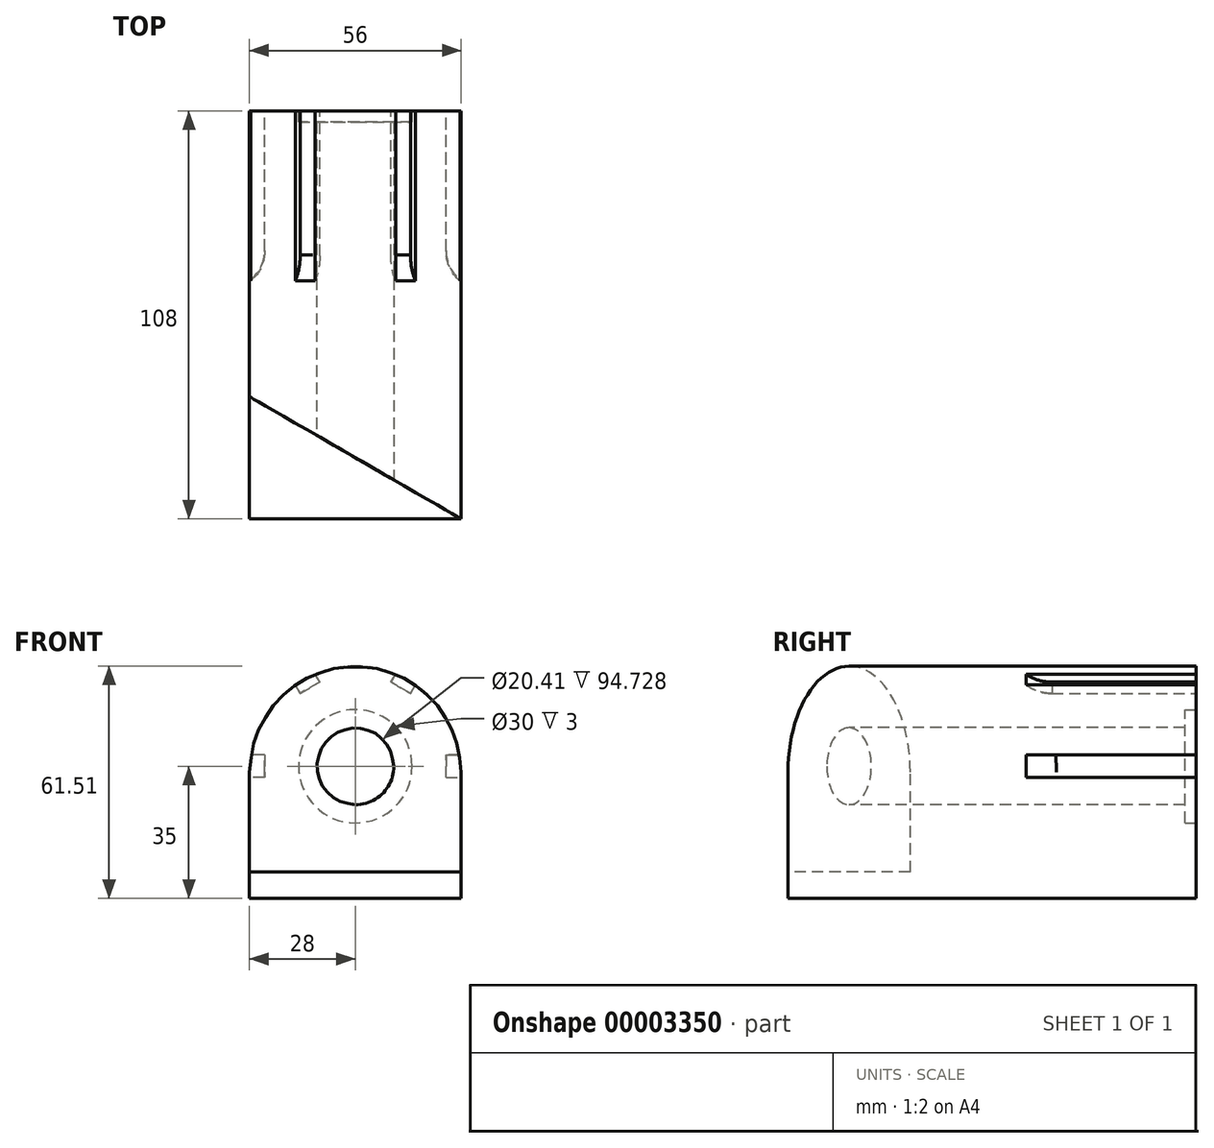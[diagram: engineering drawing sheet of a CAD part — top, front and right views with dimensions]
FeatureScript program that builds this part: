
annotation { "Feature Type Name" : "Feature", "Feature Type Description" : "" }
export const myFeature = defineFeature(function(context is Context, id is Id, definition is map)
    precondition{}
    {
        {
            var Q0;
            Q0=qCreatedBy(makeId("Front.planeOp"),FACE);
            var sketch = newSketch(context, id + "F0", { "sketchPlane" : qUnion([Q0])});
            skArc(sketch, "E0", {"start": v(28, -1.5) * mm, "mid": v(0, 26.5) * mm, "end": v(-28, -1.5) * mm});
            skLineSegment(sketch, "E1", {"start": v(-28, 0) * mm, "end": v(-28, -35) * mm});
            skLineSegment(sketch, "E2.0.MirrorCS", {"start": v(28, 0) * mm, "end": v(28, -35) * mm});
            skLineSegment(sketch, "E3", {"start": v(-28, -35) * mm, "end": v(28, -35) * mm});
            skLineSegment(sketch, "E4", {"start": v(-24, 0) * mm, "end": v(-24, -3) * mm});
            skLineSegment(sketch, "E5", {"start": v(-24, -3) * mm, "end": v(-28, -3) * mm});
            skLineSegment(sketch, "E6.0.MirrorCS", {"start": v(-24, 0) * mm, "end": v(-24, 3) * mm});
            skLineSegment(sketch, "E7.0.MirrorCS", {"start": v(-24, 3) * mm, "end": v(-27.64, 3) * mm});
            skPoint(sketch, "E8.orphan", {"position": v(-28, 3) * mm});
            skLineSegment(sketch, "E9.0.MirrorCS", {"start": v(24, 3) * mm, "end": v(27.64, 3) * mm});
            skLineSegment(sketch, "E10.0.MirrorCS", {"start": v(24, 0) * mm, "end": v(24, 3) * mm});
            skLineSegment(sketch, "E11.0.MirrorCS", {"start": v(24, 0) * mm, "end": v(24, -3) * mm});
            skLineSegment(sketch, "E12.0.MirrorCS", {"start": v(24, -3) * mm, "end": v(28, -3) * mm});
            skLineSegment(sketch, "E13", {"start": v(0, 0) * mm, "end": v(-15.25, 26.4) * mm, "construction": true});
            skLineSegment(sketch, "E14.0.MirrorCS", {"start": v(0, 0) * mm, "end": v(15.25, 26.4) * mm, "construction": true});
            skLineSegment(sketch, "E15.0.MirrorCS", {"start": v(9.4, 22.28) * mm, "end": v(10.63, 24.41) * mm});
            skLineSegment(sketch, "E16.0.MirrorCS", {"start": v(12, 20.78) * mm, "end": v(9.4, 22.28) * mm});
            skLineSegment(sketch, "E17.0.MirrorCS", {"start": v(12, 20.78) * mm, "end": v(14.6, 19.28) * mm});
            skLineSegment(sketch, "E18.0.MirrorCS", {"start": v(14.6, 19.28) * mm, "end": v(15.9, 21.55) * mm});
            skLineSegment(sketch, "E19.0.MirrorCS", {"start": v(-9.4, 22.28) * mm, "end": v(-10.63, 24.41) * mm});
            skLineSegment(sketch, "E20.0.MirrorCS", {"start": v(-12, 20.78) * mm, "end": v(-9.4, 22.28) * mm});
            skLineSegment(sketch, "E21.0.MirrorCS", {"start": v(-12, 20.78) * mm, "end": v(-14.6, 19.28) * mm});
            skLineSegment(sketch, "E22.0.MirrorCS", {"start": v(-14.6, 19.28) * mm, "end": v(-15.9, 21.55) * mm});
            skPoint(sketch, "E23.orphan", {"position": v(-16.6, 22.75) * mm});
            skPoint(sketch, "E24.orphan", {"position": v(-11.22, 25.43) * mm});
            skPoint(sketch, "E25.orphan", {"position": v(11.22, 25.43) * mm});
            skPoint(sketch, "E26.orphan", {"position": v(16.6, 22.75) * mm});
            skSolve(sketch);
        }
        {
            var Q0;
            Q0=makeQuery(id+"F0.imprint","IMPRINT",FACE,{"disambiguationData":[TD([[makeQuery(id+"F0.imprint","IMPRINT",EDGE,{"derivedFrom":sQuery(id+"F0.wireOp",EDGE,"E4")}),-1.0]])]});
            var Q1;
            {var subQ6=sQuery(id+"F0.wireOp",EDGE,"E3");Q1=makeQuery(id+"F0.imprint","IMPRINT",FACE,{"disambiguationData":[TD([[makeQuery(id+"F0.imprint","IMPRINT",EDGE,{"derivedFrom":subQ6}),1.0]])]});}
            var Q2;
            {var subQ1=sQuery(id+"F0.wireOp",EDGE,"E19.0.MirrorCS");Q2=makeQuery(id+"F0.imprint","IMPRINT",FACE,{"disambiguationData":[TD([[makeQuery(id+"F0.imprint","IMPRINT",EDGE,{"derivedFrom":subQ1}),1.0]])]});}
            var Q3;
            {var subQ1=sQuery(id+"F0.wireOp",EDGE,"E9.0.MirrorCS");Q3=makeQuery(id+"F0.imprint","IMPRINT",FACE,{"disambiguationData":[TD([[makeQuery(id+"F0.imprint","IMPRINT",EDGE,{"derivedFrom":subQ1}),-1.0]])]});}
            var Q4;
            {var subQ1=sQuery(id+"F0.wireOp",EDGE,"E15.0.MirrorCS");Q4=makeQuery(id+"F0.imprint","IMPRINT",FACE,{"disambiguationData":[TD([[makeQuery(id+"F0.imprint","IMPRINT",EDGE,{"derivedFrom":subQ1}),-1.0]])]});}
            extrude(context, id + "F1", {"entities" : qUnion([Q0, Q1, Q2, Q3, Q4]), "depth" : 108 * mm});
        }
        {
            var Q0;
            Q0=makeQuery(id+"F0.imprint","IMPRINT",FACE,{"disambiguationData":[TD([[makeQuery(id+"F0.imprint","IMPRINT",EDGE,{"derivedFrom":sQuery(id+"F0.wireOp",EDGE,"E4")}),-1.0]])]});
            var Q1;
            {var subQ1=sQuery(id+"F0.wireOp",EDGE,"E19.0.MirrorCS");Q1=makeQuery(id+"F0.imprint","IMPRINT",FACE,{"disambiguationData":[TD([[makeQuery(id+"F0.imprint","IMPRINT",EDGE,{"derivedFrom":subQ1}),1.0]])]});}
            var Q2;
            {var subQ1=sQuery(id+"F0.wireOp",EDGE,"E15.0.MirrorCS");Q2=makeQuery(id+"F0.imprint","IMPRINT",FACE,{"disambiguationData":[TD([[makeQuery(id+"F0.imprint","IMPRINT",EDGE,{"derivedFrom":subQ1}),-1.0]])]});}
            var Q3;
            {var subQ1=sQuery(id+"F0.wireOp",EDGE,"E9.0.MirrorCS");Q3=makeQuery(id+"F0.imprint","IMPRINT",FACE,{"disambiguationData":[TD([[makeQuery(id+"F0.imprint","IMPRINT",EDGE,{"derivedFrom":subQ1}),-1.0]])]});}
            extrude(context, id + "F2", {"entities" : qUnion([Q0, Q1, Q2, Q3]), "operationType" : NewBodyOperationType.REMOVE, "depth" : 45 * mm});
        }
        {
            var Q0;
            Q0=makeQuery(id+"F2.boolean.opBoolean","COPY",EDGE,{"derivedFrom":makeQuery(id+"F2.opExtrude","CAP_EDGE",EDGE,{"disambiguationData":[OSD([sQuery(id+"F0.wireOp",EDGE,"E16.0.MirrorCS"),sQuery(id+"F0.wireOp",EDGE,"E17.0.MirrorCS")])],"isStart":false})});
            var Q1;
            Q1=makeQuery(id+"F2.boolean.opBoolean","COPY",EDGE,{"derivedFrom":makeQuery(id+"F2.opExtrude","CAP_EDGE",EDGE,{"disambiguationData":[OSD([sQuery(id+"F0.wireOp",EDGE,"E10.0.MirrorCS"),sQuery(id+"F0.wireOp",EDGE,"E11.0.MirrorCS")])],"isStart":false})});
            var Q2;
            Q2=makeQuery(id+"F2.boolean.opBoolean","COPY",EDGE,{"derivedFrom":makeQuery(id+"F2.opExtrude","CAP_EDGE",EDGE,{"disambiguationData":[OSD([sQuery(id+"F0.wireOp",EDGE,"E20.0.MirrorCS"),sQuery(id+"F0.wireOp",EDGE,"E21.0.MirrorCS")])],"isStart":false})});
            var Q3;
            Q3=makeQuery(id+"F2.boolean.opBoolean","COPY",EDGE,{"derivedFrom":makeQuery(id+"F2.opExtrude","CAP_EDGE",EDGE,{"disambiguationData":[OSD([sQuery(id+"F0.wireOp",EDGE,"E4"),sQuery(id+"F0.wireOp",EDGE,"E6.0.MirrorCS")])],"isStart":false})});
            fillet(context, id + "F3", {"entities" : qUnion([Q0, Q1, Q2, Q3]), "radius" : 10 * mm, "tangentPropagation" : true, "allowEdgeOverflow" : false});
        }
        {
            var Q0;
            {var subQ6=sQuery(id+"F0.wireOp",EDGE,"E3");Q0=makeQuery(id+"F0.imprint","IMPRINT",FACE,{"disambiguationData":[TD([[makeQuery(id+"F0.imprint","IMPRINT",EDGE,{"derivedFrom":subQ6}),1.0]])]});}
            var sketch = newSketch(context, id + "F4", { "sketchPlane" : qUnion([Q0])});
            skCircle(sketch, "E27", {"center": v(0, 0) * mm, "radius": 15 * mm});
            skSolve(sketch);
        }
        {
            var Q0;
            Q0 = qSketchRegion(id + "F4", true);
            extrude(context, id + "F5", {"entities" : qUnion([Q0]), "operationType" : NewBodyOperationType.REMOVE, "depth" : 3 * mm});
        }
        {
            var Q0;
            Q0=makeQuery(id+"F1.opExtrude","CAP_FACE",FACE,{"disambiguationData":[OSD([sQuery(id+"F0.wireOp",EDGE,"E0"),sQuery(id+"F0.wireOp",EDGE,"E1"),sQuery(id+"F0.wireOp",EDGE,"E2.0.MirrorCS"),sQuery(id+"F0.wireOp",EDGE,"E3")])],"isStart":false});
            var sketch = newSketch(context, id + "F6", { "sketchPlane" : qUnion([Q0])});
            skCircle(sketch, "E28", {"center": v(0, 0) * mm, "radius": 10.2 * mm});
            skSolve(sketch);
        }
        {
            var Q0;
            Q0=makeQuery(id+"F6.imprint","IMPRINT",FACE,{"disambiguationData":[TD([[makeQuery(id+"F6.imprint","IMPRINT",EDGE,{"derivedFrom":sQuery(id+"F6.wireOp",EDGE,"E28")}),1.0]])]});
            var Q1;
            Q1=sQuery(id+"F6.wireOp",EDGE,"E28");
            extrude(context, id + "F7", {"entities" : qUnion([Q0]), "operationType" : NewBodyOperationType.REMOVE, "surfaceEntities" : qUnion([Q1]), "endBound" : BoundingType.UP_TO_NEXT, "oppositeDirection" : true, "depth" : 25 * mm});
        }
        {
            var Q0;
            Q0=qCreatedBy(makeId("Top.planeOp"),FACE);
            var sketch = newSketch(context, id + "F8", { "sketchPlane" : qUnion([Q0])});
            skLineSegment(sketch, "E29", {"start": v(28, -108) * mm, "end": v(-28, -75.67) * mm});
            skLineSegment(sketch, "E30", {"start": v(-28, -75.67) * mm, "end": v(-28, -108) * mm});
            skLineSegment(sketch, "E31", {"start": v(-28, -108) * mm, "end": v(28, -108) * mm});
            skPoint(sketch, "E32.orphan", {"position": v(49.18, -108) * mm});
            skSolve(sketch);
        }
        {
            var Q0;
            Q0=makeQuery(id+"F8.imprint","IMPRINT",FACE,{"disambiguationData":[TD([[makeQuery(id+"F8.imprint","IMPRINT",EDGE,{"derivedFrom":sQuery(id+"F8.wireOp",EDGE,"E29")}),1.0]])]});
            extrude(context, id + "F9", {"entities" : qUnion([Q0]), "operationType" : NewBodyOperationType.REMOVE, "oppositeDirection" : true, "depth" : 28 * mm});
        }
        {
            var Q0;
            Q0=makeQuery(id+"F8.imprint","IMPRINT",FACE,{"disambiguationData":[TD([[makeQuery(id+"F8.imprint","IMPRINT",EDGE,{"derivedFrom":sQuery(id+"F8.wireOp",EDGE,"E29")}),1.0]])]});
            extrude(context, id + "F10", {"entities" : qUnion([Q0]), "operationType" : NewBodyOperationType.REMOVE, "depth" : 35 * mm});
        }
    });
